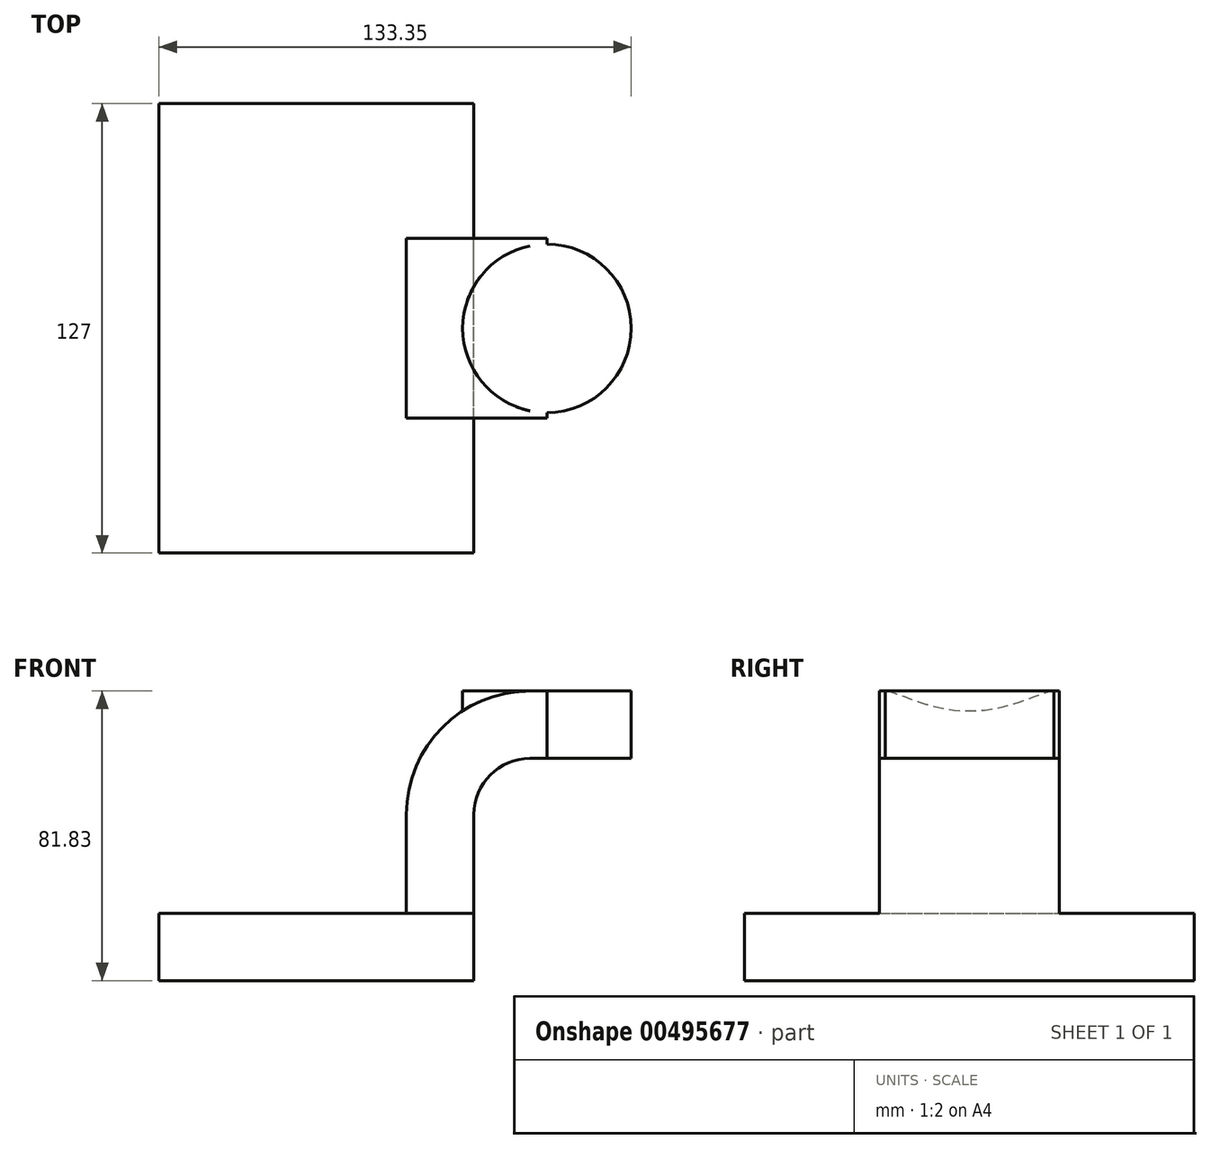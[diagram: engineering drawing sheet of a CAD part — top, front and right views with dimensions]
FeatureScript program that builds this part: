
annotation { "Feature Type Name" : "Feature", "Feature Type Description" : "" }
export const myFeature = defineFeature(function(context is Context, id is Id, definition is map)
    precondition{}
    {
        {
            var Q0;
            Q0=qCreatedBy(makeId("Front.planeOp"),FACE);
            var sketch = newSketch(context, id + "F0", { "sketchPlane" : qUnion([Q0])});
            skLineSegment(sketch, "E0.bottom", {"start": v(-44.45, 9.52) * mm, "end": v(44.45, 9.53) * mm});
            skLineSegment(sketch, "E0.top", {"start": v(-44.45, -9.53) * mm, "end": v(44.45, -9.53) * mm});
            skLineSegment(sketch, "E0.left", {"start": v(-44.45, 9.52) * mm, "end": v(-44.45, -9.53) * mm});
            skLineSegment(sketch, "E0.right", {"start": v(44.45, 9.53) * mm, "end": v(44.45, -9.52) * mm});
            skPoint(sketch, "E0.middle", {"position": v(0, 0) * mm});
            skLineSegment(sketch, "E1.bottom", {"start": v(65.1, 79.32) * mm, "end": v(115.9, 79.32) * mm});
            skLineSegment(sketch, "E1.top", {"start": v(65.1, 47.57) * mm, "end": v(115.9, 47.57) * mm});
            skLineSegment(sketch, "E1.left", {"start": v(65.1, 79.32) * mm, "end": v(65.1, 47.57) * mm});
            skLineSegment(sketch, "E1.right", {"start": v(115.9, 79.32) * mm, "end": v(115.9, 47.57) * mm});
            skPoint(sketch, "E1.middle", {"position": v(90.5, 63.45) * mm});
            skLineSegment(sketch, "E2", {"start": v(44.45, 9.53) * mm, "end": v(44.45, 37.37) * mm});
            skArc(sketch, "E3", {"start": v(44.45, 37.37) * mm, "mid": v(49.1, 48.6) * mm, "end": v(60.32, 53.25) * mm});
            skLineSegment(sketch, "E4", {"start": v(60.32, 53.25) * mm, "end": v(88.9, 53.25) * mm});
            skLineSegment(sketch, "E5.0", {"start": v(60.32, 72.3) * mm, "end": v(88.9, 72.3) * mm});
            skArc(sketch, "E5.1", {"start": v(25.4, 37.37) * mm, "mid": v(35.63, 62.07) * mm, "end": v(60.32, 72.3) * mm});
            skLineSegment(sketch, "E5.2", {"start": v(25.4, 9.53) * mm, "end": v(25.4, 37.37) * mm});
            skLineSegment(sketch, "E6", {"start": v(88.9, 79.32) * mm, "end": v(88.9, 47.57) * mm});
            skFitSpline(sketch, "E7", {"points": [v(-44.45, 9.52) * mm, v(60.32, 72.3) * mm], "startDerivative": vector(1.9, 122.9) * mm, "endDerivative": vector(117.13, -5.95) * mm});
            skSolve(sketch);
        }
        {
            var Q0;
            Q0=makeQuery(id+"F0.imprint","IMPRINT",FACE,{"disambiguationData":[TD([[makeQuery(id+"F0.imprint","IMPRINT",EDGE,{"derivedFrom":sQuery(id+"F0.wireOp",EDGE,"E0.top")}),1.0]])]});
            extrude(context, id + "F1", {"entities" : qUnion([Q0]), "endBound" : BoundingType.SYMMETRIC, "depth" : 127 * mm});
        }
        {
            var Q0;
            {var subQ1=sQuery(id+"F0.wireOp",EDGE,"E2");Q0=makeQuery(id+"F0.imprint","IMPRINT",FACE,{"disambiguationData":[TD([[makeQuery(id+"F0.imprint","IMPRINT",EDGE,{"derivedFrom":subQ1}),1.0]])]});}
            extrude(context, id + "F2", {"entities" : qUnion([Q0]), "operationType" : NewBodyOperationType.ADD, "endBound" : BoundingType.SYMMETRIC, "depth" : 50.8 * mm});
        }
        {
            var Q0;
            Q0=makeQuery(id+"F0.imprint","IMPRINT",FACE,{"disambiguationData":[TD([[makeQuery(id+"F0.imprint","IMPRINT",EDGE,{"derivedFrom":sQuery(id+"F0.wireOp",EDGE,"E5.1")}),1.0]])]});
            extrude(context, id + "F3", {"entities" : qUnion([Q0]), "operationType" : NewBodyOperationType.ADD, "endBound" : BoundingType.SYMMETRIC, "depth" : 15.88 * mm});
        }
        {
            var Q0;
            {var subQ0=sQuery(id+"F0.wireOp",EDGE,"E5.0");var subQ1=sQuery(id+"F0.wireOp",EDGE,"E1.left");var subQ2=makeQuery(id+"F0.imprint","INTERSECT",VERTEX,{"derivedFrom":[subQ1,subQ0]});Q0=makeQuery(id+"F0.imprint","IMPRINT",FACE,{"disambiguationData":[TD([[makeQuery(id+"F0.imprint","IMPRINT",EDGE,{"disambiguationData":[TD([[subQ2,-1.0]])],"derivedFrom":subQ1}),1.0]])]});}
            var Q1;
            Q1=sQuery(id+"F0.wireOp",EDGE,"E1.left");
            revolve(context, id + "F4", {"operationType" : NewBodyOperationType.ADD, "entities" : qUnion([Q0]), "axis" : qUnion([Q1]), "revolveType" : RevolveType.FULL});
        }
    });
